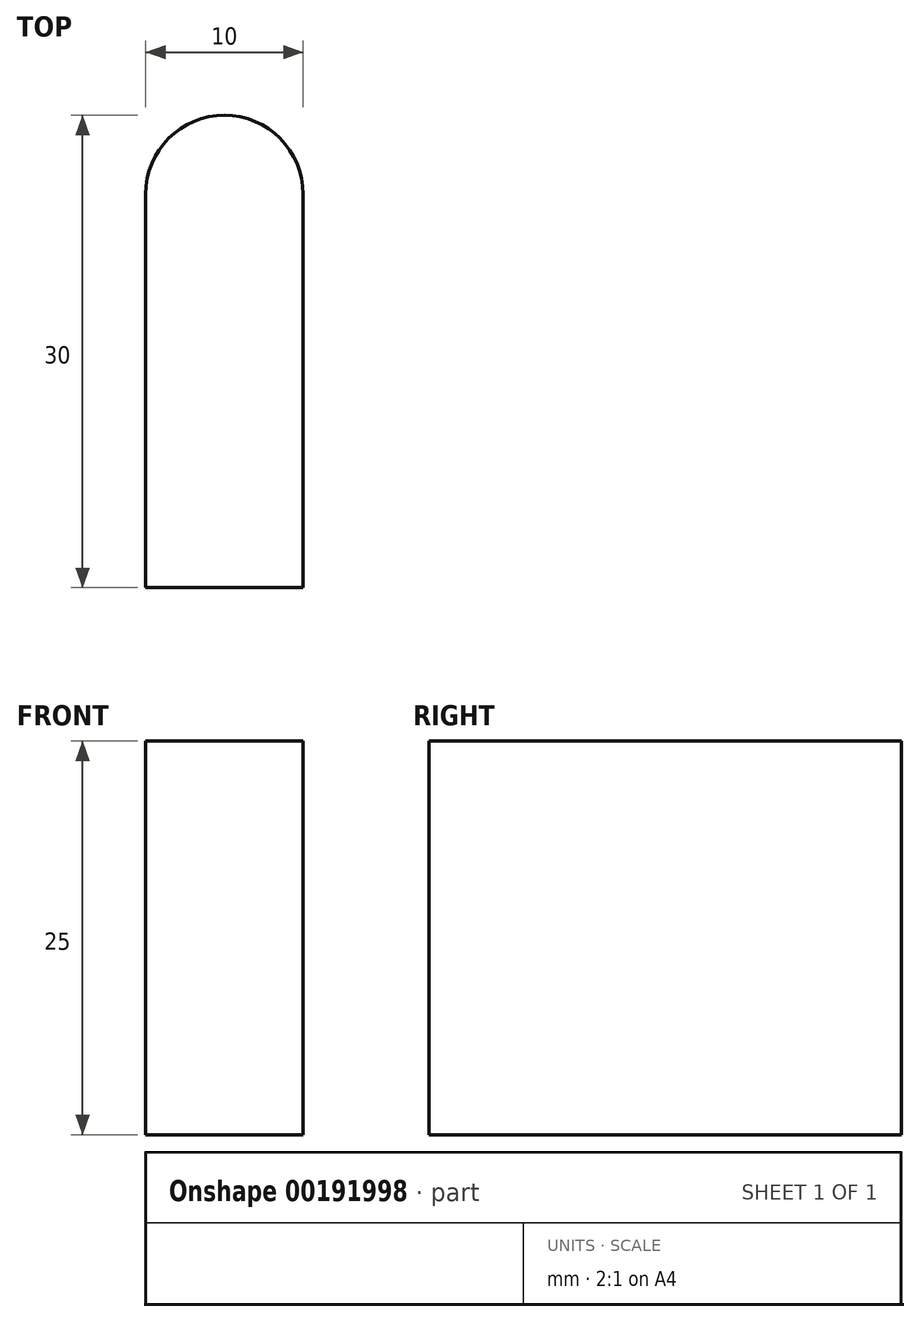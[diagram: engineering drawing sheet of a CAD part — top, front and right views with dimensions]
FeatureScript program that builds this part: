
annotation { "Feature Type Name" : "Feature", "Feature Type Description" : "" }
export const myFeature = defineFeature(function(context is Context, id is Id, definition is map)
    precondition{}
    {
        {
            var Q0;
            Q0=qCreatedBy(makeId("Top.planeOp"),FACE);
            var sketch = newSketch(context, id + "F0", { "sketchPlane" : qUnion([Q0])});
            skLineSegment(sketch, "E0.bottom", {"start": v(5, -15) * mm, "end": v(-5, -15) * mm});
            skLineSegment(sketch, "E0.top", {"start": v(0, 15) * mm, "end": v(0, 15) * mm});
            skLineSegment(sketch, "E0.left", {"start": v(5, -15) * mm, "end": v(5, 10) * mm});
            skLineSegment(sketch, "E0.right", {"start": v(-5, -15) * mm, "end": v(-5, 10) * mm});
            skPoint(sketch, "E0.middle", {"position": v(0, 0) * mm});
            skPoint(sketch, "E1.visualSharp", {"position": v(-5, 15) * mm});
            skArc(sketch, "E1.filletArc", {"start": v(0, 15) * mm, "mid": v(-3.54, 13.54) * mm, "end": v(-5, 10) * mm});
            skPoint(sketch, "E2.visualSharp", {"position": v(5, 15) * mm});
            skArc(sketch, "E2.filletArc", {"start": v(5, 10) * mm, "mid": v(3.54, 13.54) * mm, "end": v(0, 15) * mm});
            skSolve(sketch);
        }
        {
            var Q0;
            Q0=makeQuery(id+"F0.imprint","IMPRINT",FACE,{"disambiguationData":[TD([[makeQuery(id+"F0.imprint","IMPRINT",EDGE,{"derivedFrom":sQuery(id+"F0.wireOp",EDGE,"E0.bottom")}),-1.0]])]});
            extrude(context, id + "F1", {"entities" : qUnion([Q0]), "depth" : 25 * mm});
        }
    });
